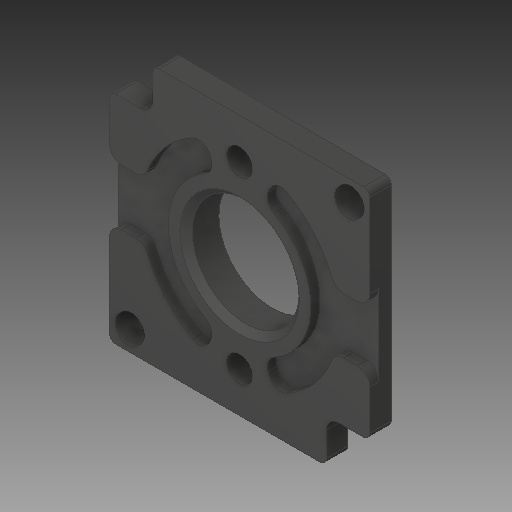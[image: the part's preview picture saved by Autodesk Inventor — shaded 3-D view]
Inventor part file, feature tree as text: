
AUTODESK INVENTOR PART (.ipt)
format: ipt  version: 2017 (Build 210142000, 142)  size: 294,400 bytes
history: native  units: in
note: dims shown in document units (in); Inventor stores cm internally (conversion verified against a paired STEP export)
features: fillet x1
ambient origin geometry x8: Origin, YZ Plane, XZ Plane, XY Plane, X Axis, Y Axis, Z Axis, Center Point
bodies: Solid1 (feature_tree)
feature tree (1):
  fillet  "Fillet4"  [1 undecoded]
note: 1 required parameter value undecoded (feature->parameter linkage not recoverable at this tier; creation-order binding heuristic only, values carry confidence <= 0.55)
